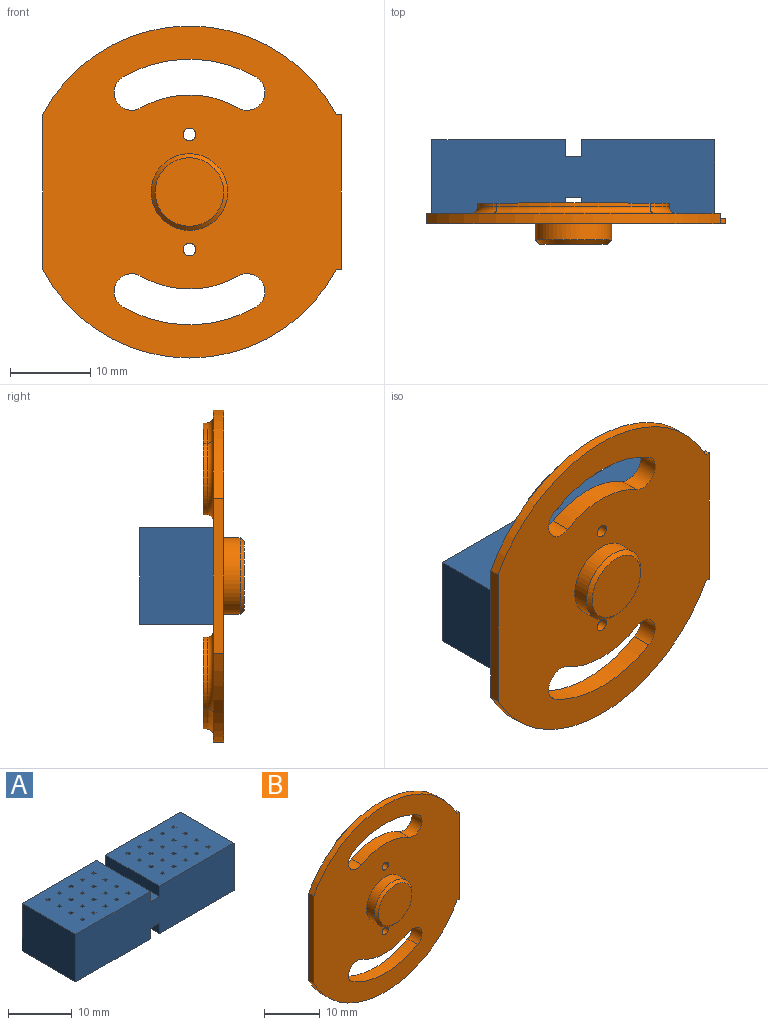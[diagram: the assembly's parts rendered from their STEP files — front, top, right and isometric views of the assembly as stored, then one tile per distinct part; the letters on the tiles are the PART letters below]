
ASSEMBLY  parts=2 mates=1
PART A: 214 faces, bbox 35.2x11.9x9.1 mm
  f0: plane 2.03x0.51mm, normal (0,1,0), area 1mm2, adj f1,f3,f4,f194
  f1: plane 2.03x0.51mm, normal (1,0,0), area 1mm2, adj f0,f2,f4,f194
  f2: plane 2.03x0.51mm, normal (0,-1,0), area 1mm2, adj f1,f3,f4,f194
  f3: plane 2.03x0.51mm, normal (-1,0,0), area 1mm2, adj f0,f2,f4,f194
  f4: plane 0.51x0.51mm, normal (0,0,1), area 0.3mm2, adj f0,f1,f2,f3
  f5: plane 2.03x0.51mm, normal (0,1,0), area 1mm2, adj f6,f8,f9,f194
  f6: plane 2.03x0.51mm, normal (1,0,0), area 1mm2, adj f5,f7,f9,f194
  f7: plane 2.03x0.51mm, normal (0,-1,0), area 1mm2, adj f6,f8,f9,f194
  f8: plane 2.03x0.51mm, normal (-1,0,0), area 1mm2, adj f5,f7,f9,f194
  f9: plane 0.51x0.51mm, normal (0,0,1), area 0.3mm2, adj f5,f6,f7,f8
  f10: plane 2.03x0.51mm, normal (0,1,0), area 1mm2, adj f11,f13,f14,f194
  f11: plane 2.03x0.51mm, normal (1,0,0), area 1mm2, adj f10,f12,f14,f194
  f12: plane 2.03x0.51mm, normal (0,-1,0), area 1mm2, adj f11,f13,f14,f194
  f13: plane 2.03x0.51mm, normal (-1,0,0), area 1mm2, adj f10,f12,f14,f194
  f14: plane 0.51x0.51mm, normal (0,0,1), area 0.3mm2, adj f10,f11,f12,f13
  f15: plane 2.03x0.51mm, normal (0,1,0), area 1mm2, adj f16,f18,f19,f194
  f16: plane 2.03x0.51mm, normal (1,0,0), area 1mm2, adj f15,f17,f19,f194
  f17: plane 2.03x0.51mm, normal (0,-1,0), area 1mm2, adj f16,f18,f19,f194
  f18: plane 2.03x0.51mm, normal (-1,0,0), area 1mm2, adj f15,f17,f19,f194
  f19: plane 0.51x0.51mm, normal (0,0,1), area 0.3mm2, adj f15,f16,f17,f18
  f20: plane 2.03x0.51mm, normal (0,1,0), area 1mm2, adj f21,f23,f24,f194
  f21: plane 2.03x0.51mm, normal (1,0,0), area 1mm2, adj f20,f22,f24,f194
  f22: plane 2.03x0.51mm, normal (0,-1,0), area 1mm2, adj f21,f23,f24,f194
  f23: plane 2.03x0.51mm, normal (-1,0,0), area 1mm2, adj f20,f22,f24,f194
  f24: plane 0.51x0.51mm, normal (0,0,1), area 0.3mm2, adj f20,f21,f22,f23
  f25: plane 2.03x0.51mm, normal (0,1,0), area 1mm2, adj f26,f28,f29,f194
  f26: plane 2.03x0.51mm, normal (1,0,0), area 1mm2, adj f25,f27,f29,f194
  f27: plane 2.03x0.51mm, normal (0,-1,0), area 1mm2, adj f26,f28,f29,f194
  f28: plane 2.03x0.51mm, normal (-1,0,0), area 1mm2, adj f25,f27,f29,f194
  f29: plane 0.51x0.51mm, normal (0,0,1), area 0.3mm2, adj f25,f26,f27,f28
  f30: plane 2.03x0.51mm, normal (0,1,0), area 1mm2, adj f31,f33,f34,f194
  f31: plane 2.03x0.51mm, normal (1,0,0), area 1mm2, adj f30,f32,f34,f194
  f32: plane 2.03x0.51mm, normal (0,-1,0), area 1mm2, adj f31,f33,f34,f194
  f33: plane 2.03x0.51mm, normal (-1,0,0), area 1mm2, adj f30,f32,f34,f194
  f34: plane 0.51x0.51mm, normal (0,0,1), area 0.3mm2, adj f30,f31,f32,f33
  f35: plane 2.03x0.51mm, normal (0,1,0), area 1mm2, adj f36,f38,f39,f194
  f36: plane 2.03x0.51mm, normal (1,0,0), area 1mm2, adj f35,f37,f39,f194
  f37: plane 2.03x0.51mm, normal (0,-1,0), area 1mm2, adj f36,f38,f39,f194
  f38: plane 2.03x0.51mm, normal (-1,0,0), area 1mm2, adj f35,f37,f39,f194
  f39: plane 0.51x0.51mm, normal (0,0,1), area 0.3mm2, adj f35,f36,f37,f38
  f40: plane 2.03x0.51mm, normal (0,1,0), area 1mm2, adj f41,f43,f44,f194
  f41: plane 2.03x0.51mm, normal (1,0,0), area 1mm2, adj f40,f42,f44,f194
  f42: plane 2.03x0.51mm, normal (0,-1,0), area 1mm2, adj f41,f43,f44,f194
  f43: plane 2.03x0.51mm, normal (-1,0,0), area 1mm2, adj f40,f42,f44,f194
  f44: plane 0.51x0.51mm, normal (0,0,1), area 0.3mm2, adj f40,f41,f42,f43
  f45: plane 2.03x0.51mm, normal (0,1,0), area 1mm2, adj f46,f48,f49,f194
  f46: plane 2.03x0.51mm, normal (1,0,0), area 1mm2, adj f45,f47,f49,f194
  f47: plane 2.03x0.51mm, normal (0,-1,0), area 1mm2, adj f46,f48,f49,f194
  f48: plane 2.03x0.51mm, normal (-1,0,0), area 1mm2, adj f45,f47,f49,f194
  f49: plane 0.51x0.51mm, normal (0,0,1), area 0.3mm2, adj f45,f46,f47,f48
  f50: plane 2.03x0.51mm, normal (0,1,0), area 1mm2, adj f51,f53,f54,f194
  f51: plane 2.03x0.51mm, normal (1,0,0), area 1mm2, adj f50,f52,f54,f194
  f52: plane 2.03x0.51mm, normal (0,-1,0), area 1mm2, adj f51,f53,f54,f194
  f53: plane 2.03x0.51mm, normal (-1,0,0), area 1mm2, adj f50,f52,f54,f194
  f54: plane 0.51x0.51mm, normal (0,0,1), area 0.3mm2, adj f50,f51,f52,f53
  f55: plane 2.03x0.51mm, normal (0,1,0), area 1mm2, adj f56,f58,f59,f194
  f56: plane 2.03x0.51mm, normal (1,0,0), area 1mm2, adj f55,f57,f59,f194
  f57: plane 2.03x0.51mm, normal (0,-1,0), area 1mm2, adj f56,f58,f59,f194
  f58: plane 2.03x0.51mm, normal (-1,0,0), area 1mm2, adj f55,f57,f59,f194
  f59: plane 0.51x0.51mm, normal (0,0,1), area 0.3mm2, adj f55,f56,f57,f58
  f60: plane 2.03x0.51mm, normal (0,1,0), area 1mm2, adj f61,f63,f64,f194
  f61: plane 2.03x0.51mm, normal (1,0,0), area 1mm2, adj f60,f62,f64,f194
  f62: plane 2.03x0.51mm, normal (0,-1,0), area 1mm2, adj f61,f63,f64,f194
  f63: plane 2.03x0.51mm, normal (-1,0,0), area 1mm2, adj f60,f62,f64,f194
  f64: plane 0.51x0.51mm, normal (0,0,1), area 0.3mm2, adj f60,f61,f62,f63
  f65: plane 2.03x0.51mm, normal (0,1,0), area 1mm2, adj f66,f68,f69,f194
  f66: plane 2.03x0.51mm, normal (1,0,0), area 1mm2, adj f65,f67,f69,f194
  f67: plane 2.03x0.51mm, normal (0,-1,0), area 1mm2, adj f66,f68,f69,f194
  f68: plane 2.03x0.51mm, normal (-1,0,0), area 1mm2, adj f65,f67,f69,f194
  f69: plane 0.51x0.51mm, normal (0,0,1), area 0.3mm2, adj f65,f66,f67,f68
  f70: plane 2.03x0.51mm, normal (0,1,0), area 1mm2, adj f71,f73,f74,f194
  f71: plane 2.03x0.51mm, normal (1,0,0), area 1mm2, adj f70,f72,f74,f194
  f72: plane 2.03x0.51mm, normal (0,-1,0), area 1mm2, adj f71,f73,f74,f194
  f73: plane 2.03x0.51mm, normal (-1,0,0), area 1mm2, adj f70,f72,f74,f194
  f74: plane 0.51x0.51mm, normal (0,0,1), area 0.3mm2, adj f70,f71,f72,f73
  f75: plane 2.03x0.51mm, normal (0,1,0), area 1mm2, adj f76,f78,f79,f194
  f76: plane 2.03x0.51mm, normal (1,0,0), area 1mm2, adj f75,f77,f79,f194
  f77: plane 2.03x0.51mm, normal (0,-1,0), area 1mm2, adj f76,f78,f79,f194
  f78: plane 2.03x0.51mm, normal (-1,0,0), area 1mm2, adj f75,f77,f79,f194
  f79: plane 0.51x0.51mm, normal (0,0,1), area 0.3mm2, adj f75,f76,f77,f78
  f80: plane 2.03x0.51mm, normal (0,1,0), area 1mm2, adj f81,f83,f84,f194
  f81: plane 2.03x0.51mm, normal (1,0,0), area 1mm2, adj f80,f82,f84,f194
  f82: plane 2.03x0.51mm, normal (0,-1,0), area 1mm2, adj f81,f83,f84,f194
  f83: plane 2.03x0.51mm, normal (-1,0,0), area 1mm2, adj f80,f82,f84,f194
  f84: plane 0.51x0.51mm, normal (0,0,1), area 0.3mm2, adj f80,f81,f82,f83
  f85: plane 2.03x0.51mm, normal (0,1,0), area 1mm2, adj f86,f88,f89,f194
  f86: plane 2.03x0.51mm, normal (1,0,0), area 1mm2, adj f85,f87,f89,f194
  f87: plane 2.03x0.51mm, normal (0,-1,0), area 1mm2, adj f86,f88,f89,f194
  f88: plane 2.03x0.51mm, normal (-1,0,0), area 1mm2, adj f85,f87,f89,f194
  f89: plane 0.51x0.51mm, normal (0,0,1), area 0.3mm2, adj f85,f86,f87,f88
  f90: plane 2.03x0.51mm, normal (0,1,0), area 1mm2, adj f91,f93,f94,f194
  f91: plane 2.03x0.51mm, normal (1,0,0), area 1mm2, adj f90,f92,f94,f194
  f92: plane 2.03x0.51mm, normal (0,-1,0), area 1mm2, adj f91,f93,f94,f194
  f93: plane 2.03x0.51mm, normal (-1,0,0), area 1mm2, adj f90,f92,f94,f194
  f94: plane 0.51x0.51mm, normal (0,0,1), area 0.3mm2, adj f90,f91,f92,f93
  f95: plane 2.03x0.51mm, normal (0,1,0), area 1mm2, adj f96,f98,f99,f190
  f96: plane 2.03x0.51mm, normal (-1,0,0), area 1mm2, adj f95,f97,f99,f190
  f97: plane 2.03x0.51mm, normal (0,-1,0), area 1mm2, adj f96,f98,f99,f190
  f98: plane 2.03x0.51mm, normal (1,0,0), area 1mm2, adj f95,f97,f99,f190
  f99: plane 0.51x0.51mm, normal (0,0,1), area 0.3mm2, adj f95,f96,f97,f98
  f100: plane 2.03x0.51mm, normal (0,1,0), area 1mm2, adj f101,f103,f104,f190
  f101: plane 2.03x0.51mm, normal (-1,0,0), area 1mm2, adj f100,f102,f104,f190
  f102: plane 2.03x0.51mm, normal (0,-1,0), area 1mm2, adj f101,f103,f104,f190
  f103: plane 2.03x0.51mm, normal (1,0,0), area 1mm2, adj f100,f102,f104,f190
  f104: plane 0.51x0.51mm, normal (0,0,1), area 0.3mm2, adj f100,f101,f102,f103
  f105: plane 2.03x0.51mm, normal (0,1,0), area 1mm2, adj f106,f108,f109,f190
  f106: plane 2.03x0.51mm, normal (-1,0,0), area 1mm2, adj f105,f107,f109,f190
  f107: plane 2.03x0.51mm, normal (0,-1,0), area 1mm2, adj f106,f108,f109,f190
  f108: plane 2.03x0.51mm, normal (1,0,0), area 1mm2, adj f105,f107,f109,f190
  f109: plane 0.51x0.51mm, normal (0,0,1), area 0.3mm2, adj f105,f106,f107,f108
  f110: plane 2.03x0.51mm, normal (0,1,0), area 1mm2, adj f111,f113,f114,f190
  f111: plane 2.03x0.51mm, normal (-1,0,0), area 1mm2, adj f110,f112,f114,f190
  f112: plane 2.03x0.51mm, normal (0,-1,0), area 1mm2, adj f111,f113,f114,f190
  f113: plane 2.03x0.51mm, normal (1,0,0), area 1mm2, adj f110,f112,f114,f190
  f114: plane 0.51x0.51mm, normal (0,0,1), area 0.3mm2, adj f110,f111,f112,f113
  f115: plane 2.03x0.51mm, normal (0,1,0), area 1mm2, adj f116,f118,f119,f190
  f116: plane 2.03x0.51mm, normal (-1,0,0), area 1mm2, adj f115,f117,f119,f190
  f117: plane 2.03x0.51mm, normal (0,-1,0), area 1mm2, adj f116,f118,f119,f190
  f118: plane 2.03x0.51mm, normal (1,0,0), area 1mm2, adj f115,f117,f119,f190
  f119: plane 0.51x0.51mm, normal (0,0,1), area 0.3mm2, adj f115,f116,f117,f118
  f120: plane 2.03x0.51mm, normal (0,1,0), area 1mm2, adj f121,f123,f124,f190
  f121: plane 2.03x0.51mm, normal (-1,0,0), area 1mm2, adj f120,f122,f124,f190
  f122: plane 2.03x0.51mm, normal (0,-1,0), area 1mm2, adj f121,f123,f124,f190
  f123: plane 2.03x0.51mm, normal (1,0,0), area 1mm2, adj f120,f122,f124,f190
  f124: plane 0.51x0.51mm, normal (0,0,1), area 0.3mm2, adj f120,f121,f122,f123
  f125: plane 2.03x0.51mm, normal (0,1,0), area 1mm2, adj f126,f128,f129,f190
  f126: plane 2.03x0.51mm, normal (-1,0,0), area 1mm2, adj f125,f127,f129,f190
  f127: plane 2.03x0.51mm, normal (0,-1,0), area 1mm2, adj f126,f128,f129,f190
  f128: plane 2.03x0.51mm, normal (1,0,0), area 1mm2, adj f125,f127,f129,f190
  f129: plane 0.51x0.51mm, normal (0,0,1), area 0.3mm2, adj f125,f126,f127,f128
  f130: plane 2.03x0.51mm, normal (0,1,0), area 1mm2, adj f131,f133,f134,f190
  f131: plane 2.03x0.51mm, normal (-1,0,0), area 1mm2, adj f130,f132,f134,f190
  f132: plane 2.03x0.51mm, normal (0,-1,0), area 1mm2, adj f131,f133,f134,f190
  f133: plane 2.03x0.51mm, normal (1,0,0), area 1mm2, adj f130,f132,f134,f190
  f134: plane 0.51x0.51mm, normal (0,0,1), area 0.3mm2, adj f130,f131,f132,f133
  f135: plane 2.03x0.51mm, normal (0,1,0), area 1mm2, adj f136,f138,f139,f190
  f136: plane 2.03x0.51mm, normal (-1,0,0), area 1mm2, adj f135,f137,f139,f190
  f137: plane 2.03x0.51mm, normal (0,-1,0), area 1mm2, adj f136,f138,f139,f190
  f138: plane 2.03x0.51mm, normal (1,0,0), area 1mm2, adj f135,f137,f139,f190
  f139: plane 0.51x0.51mm, normal (0,0,1), area 0.3mm2, adj f135,f136,f137,f138
  f140: plane 2.03x0.51mm, normal (0,1,0), area 1mm2, adj f141,f143,f144,f190
  f141: plane 2.03x0.51mm, normal (-1,0,0), area 1mm2, adj f140,f142,f144,f190
  f142: plane 2.03x0.51mm, normal (0,-1,0), area 1mm2, adj f141,f143,f144,f190
  f143: plane 2.03x0.51mm, normal (1,0,0), area 1mm2, adj f140,f142,f144,f190
  f144: plane 0.51x0.51mm, normal (0,0,1), area 0.3mm2, adj f140,f141,f142,f143
  f145: plane 2.03x0.51mm, normal (0,1,0), area 1mm2, adj f146,f148,f149,f190
  f146: plane 2.03x0.51mm, normal (-1,0,0), area 1mm2, adj f145,f147,f149,f190
  f147: plane 2.03x0.51mm, normal (0,-1,0), area 1mm2, adj f146,f148,f149,f190
  f148: plane 2.03x0.51mm, normal (1,0,0), area 1mm2, adj f145,f147,f149,f190
  f149: plane 0.51x0.51mm, normal (0,0,1), area 0.3mm2, adj f145,f146,f147,f148
  f150: plane 2.03x0.51mm, normal (0,1,0), area 1mm2, adj f151,f153,f154,f190
  f151: plane 2.03x0.51mm, normal (-1,0,0), area 1mm2, adj f150,f152,f154,f190
  f152: plane 2.03x0.51mm, normal (0,-1,0), area 1mm2, adj f151,f153,f154,f190
  f153: plane 2.03x0.51mm, normal (1,0,0), area 1mm2, adj f150,f152,f154,f190
  f154: plane 0.51x0.51mm, normal (0,0,1), area 0.3mm2, adj f150,f151,f152,f153
  f155: plane 2.03x0.51mm, normal (0,1,0), area 1mm2, adj f156,f158,f159,f190
  f156: plane 2.03x0.51mm, normal (-1,0,0), area 1mm2, adj f155,f157,f159,f190
  f157: plane 2.03x0.51mm, normal (0,-1,0), area 1mm2, adj f156,f158,f159,f190
  f158: plane 2.03x0.51mm, normal (1,0,0), area 1mm2, adj f155,f157,f159,f190
  f159: plane 0.51x0.51mm, normal (0,0,1), area 0.3mm2, adj f155,f156,f157,f158
  f160: plane 2.03x0.51mm, normal (0,1,0), area 1mm2, adj f161,f163,f164,f190
  f161: plane 2.03x0.51mm, normal (-1,0,0), area 1mm2, adj f160,f162,f164,f190
  f162: plane 2.03x0.51mm, normal (0,-1,0), area 1mm2, adj f161,f163,f164,f190
  f163: plane 2.03x0.51mm, normal (1,0,0), area 1mm2, adj f160,f162,f164,f190
  f164: plane 0.51x0.51mm, normal (0,0,1), area 0.3mm2, adj f160,f161,f162,f163
  f165: plane 2.03x0.51mm, normal (0,1,0), area 1mm2, adj f166,f168,f169,f190
  f166: plane 2.03x0.51mm, normal (-1,0,0), area 1mm2, adj f165,f167,f169,f190
  f167: plane 2.03x0.51mm, normal (0,-1,0), area 1mm2, adj f166,f168,f169,f190
  f168: plane 2.03x0.51mm, normal (1,0,0), area 1mm2, adj f165,f167,f169,f190
  f169: plane 0.51x0.51mm, normal (0,0,1), area 0.3mm2, adj f165,f166,f167,f168
  f170: plane 2.03x0.51mm, normal (0,1,0), area 1mm2, adj f171,f173,f174,f190
  f171: plane 2.03x0.51mm, normal (-1,0,0), area 1mm2, adj f170,f172,f174,f190
  f172: plane 2.03x0.51mm, normal (0,-1,0), area 1mm2, adj f171,f173,f174,f190
  f173: plane 2.03x0.51mm, normal (1,0,0), area 1mm2, adj f170,f172,f174,f190
  f174: plane 0.51x0.51mm, normal (0,0,1), area 0.3mm2, adj f170,f171,f172,f173
  f175: plane 2.03x0.51mm, normal (0,1,0), area 1mm2, adj f176,f178,f179,f190
  f176: plane 2.03x0.51mm, normal (-1,0,0), area 1mm2, adj f175,f177,f179,f190
  f177: plane 2.03x0.51mm, normal (0,-1,0), area 1mm2, adj f176,f178,f179,f190
  f178: plane 2.03x0.51mm, normal (1,0,0), area 1mm2, adj f175,f177,f179,f190
  f179: plane 0.51x0.51mm, normal (0,0,1), area 0.3mm2, adj f175,f176,f177,f178
  f180: plane 2.03x0.51mm, normal (0,1,0), area 1mm2, adj f181,f183,f184,f190
  f181: plane 2.03x0.51mm, normal (-1,0,0), area 1mm2, adj f180,f182,f184,f190
  f182: plane 2.03x0.51mm, normal (0,-1,0), area 1mm2, adj f181,f183,f184,f190
  f183: plane 2.03x0.51mm, normal (1,0,0), area 1mm2, adj f180,f182,f184,f190
  f184: plane 0.51x0.51mm, normal (0,0,1), area 0.3mm2, adj f180,f181,f182,f183
  f185: plane 2.03x0.51mm, normal (0,1,0), area 1mm2, adj f186,f188,f189,f190
  f186: plane 2.03x0.51mm, normal (-1,0,0), area 1mm2, adj f185,f187,f189,f190
  f187: plane 2.03x0.51mm, normal (0,-1,0), area 1mm2, adj f186,f188,f189,f190
  f188: plane 2.03x0.51mm, normal (1,0,0), area 1mm2, adj f185,f187,f189,f190
  f189: plane 0.51x0.51mm, normal (0,0,1), area 0.3mm2, adj f185,f186,f187,f188
  f190: plane 16.57x11.94mm, normal (0,0,1), area 192.7mm2, adj f95,f96,f97,f98,f100,f101,f102,f103
  f191: plane 16.57x11.94mm, normal (0,0,-1), area 197.9mm2, adj f195,f196,f197,f203
  f192: plane 16.57x11.94mm, normal (0,0,-1), area 197.9mm2, adj f193,f196,f197,f201
  f193: plane 11.94x9.14mm, normal (1,0,0), area 109.2mm2, adj f192,f194,f196,f197
  f194: plane 16.57x11.94mm, normal (0,0,1), area 192.7mm2, adj f0,f1,f2,f3,f5,f6,f7,f8
  f195: plane 11.94x9.14mm, normal (-1,0,0), area 109.2mm2, adj f190,f191,f196,f197
  f196: plane 35.18x9.14mm, normal (0,-1,0), area 313.4mm2, adj f190,f191,f192,f193,f194,f195,f198,f199
  f197: plane 35.18x9.14mm, normal (0,1,0), area 313.4mm2, adj f190,f191,f192,f193,f194,f195,f198,f199
  f198: plane 11.94x2.03mm, normal (1,0,0), area 24.3mm2, adj f190,f196,f197,f199
  f199: plane 11.94x2.03mm, normal (0,0,1), area 24.3mm2, adj f196,f197,f198,f200
  f200: plane 11.94x2.03mm, normal (-1,0,0), area 24.3mm2, adj f194,f196,f197,f199
  f201: plane 11.94x2.03mm, normal (-1,0,0), area 24.3mm2, adj f192,f196,f197,f202
  f202: plane 11.94x2.03mm, normal (0,0,-1), area 24.3mm2, adj f196,f197,f201,f203
  f203: plane 11.94x2.03mm, normal (1,0,0), area 24.3mm2, adj f191,f196,f197,f202
  f204: plane 2.03x0.51mm, normal (0,1,0), area 1mm2, adj f190,f205,f207,f208
  f205: plane 2.03x0.51mm, normal (-1,0,0), area 1mm2, adj f190,f204,f206,f208
  f206: plane 2.03x0.51mm, normal (0,-1,0), area 1mm2, adj f190,f205,f207,f208
  f207: plane 2.03x0.51mm, normal (1,0,0), area 1mm2, adj f190,f204,f206,f208
  f208: plane 0.51x0.51mm, normal (0,0,1), area 0.3mm2, adj f204,f205,f206,f207
  f209: plane 2.03x0.51mm, normal (0,1,0), area 1mm2, adj f194,f210,f212,f213
  f210: plane 2.03x0.51mm, normal (-1,0,0), area 1mm2, adj f194,f209,f211,f213
  f211: plane 2.03x0.51mm, normal (0,-1,0), area 1mm2, adj f194,f210,f212,f213
  f212: plane 2.03x0.51mm, normal (1,0,0), area 1mm2, adj f194,f209,f211,f213
  f213: plane 0.51x0.51mm, normal (0,0,1), area 0.3mm2, adj f209,f210,f211,f212
PART B: 41 faces, bbox 37.1x5.2x44.2 mm
  f0: plane 19.25x0.64mm, normal (1,0,0), area 12.2mm2, adj f1,f3,f4,f37
  f1: cylinder r=20.64mm len=36.51mm, axis (0,1,0), area 56.9mm2, adj f0,f2,f3,f35,f39
  f2: plane 41.28x37.15mm, normal (0,-1,0), area 1049.1mm2, adj f1,f4,f5,f7,f14,f15,f16,f17
  f3: plane 41.28x36.51mm, normal (0,1,0), area 745.7mm2, adj f0,f1,f4,f5,f18,f19,f20,f21
  f4: cylinder r=20.64mm len=36.51mm, axis (0,1,0), area 56.9mm2, adj f0,f2,f3,f35,f38
  f5: cylinder r=0.79mm len=1.59mm, axis (0,1,0), area 6.3mm2, adj f2,f3
  f6: plane 23.81x11.44mm, normal (0,1,0), area 131.7mm2, adj f22,f23,f24,f25,f26,f27,f28,f29
  f7: cylinder r=4.76mm len=9.53mm, axis (0,1,0), area 60.8mm2, adj f2,f36
  f8: plane 8.51x8.51mm, normal (0,-1,0), area 56.9mm2, adj f36
  f9: cylinder r=19.05mm len=19.05mm, axis (0,-1,0), area 9.5mm2, adj f10,f12,f13,f21
  f10: cylinder r=4.76mm len=8.89mm, axis (0,-1,0), area 7.1mm2, adj f9,f11,f13,f19
  f11: cylinder r=9.53mm len=9.53mm, axis (0,-1,0), area 4.8mm2, adj f10,f12,f13,f18
  f12: cylinder r=4.76mm len=8.89mm, axis (0,-1,0), area 7.1mm2, adj f9,f11,f13,f20
  f13: plane 23.81x11.44mm, normal (0,1,0), area 131.7mm2, adj f9,f10,f11,f12,f14,f15,f16,f17
  f14: cylinder r=2.22mm len=4.15mm, axis (0,1,0), area 17.7mm2, adj f2,f13,f15,f16
  f15: cylinder r=16.51mm len=16.51mm, axis (0,1,0), area 43.9mm2, adj f2,f13,f14,f17
  f16: cylinder r=12.06mm len=12.07mm, axis (0,1,0), area 32.1mm2, adj f2,f13,f14,f17
  f17: cylinder r=2.22mm len=4.15mm, axis (0,1,0), area 17.7mm2, adj f2,f13,f15,f16
  f18: torus R=8.73mm, axis (0,-1,0), area 12.1mm2, adj f3,f11,f19,f20
  f19: torus R=5.56mm, axis (0,-1,0), area 19.8mm2, adj f3,f10,f18,f21
  f20: torus R=5.56mm, axis (0,-1,0), area 19.8mm2, adj f3,f12,f18,f21
  f21: torus R=19.84mm, axis (0,-1,0), area 25.2mm2, adj f3,f9,f19,f20
  f22: cylinder r=19.05mm len=19.05mm, axis (0,-1,0), area 9.5mm2, adj f6,f23,f25,f33
  f23: cylinder r=4.76mm len=8.89mm, axis (0,-1,0), area 7.1mm2, adj f6,f22,f24,f32
  f24: cylinder r=9.53mm len=9.53mm, axis (0,-1,0), area 4.8mm2, adj f6,f23,f25,f30
  f25: cylinder r=4.76mm len=8.89mm, axis (0,-1,0), area 7.1mm2, adj f6,f22,f24,f31
  f26: cylinder r=16.51mm len=16.51mm, axis (0,1,0), area 43.9mm2, adj f2,f6,f27,f29
  f27: cylinder r=2.22mm len=4.15mm, axis (0,1,0), area 17.7mm2, adj f2,f6,f26,f28
  f28: cylinder r=12.06mm len=12.07mm, axis (0,1,0), area 32.1mm2, adj f2,f6,f27,f29
  f29: cylinder r=2.22mm len=4.15mm, axis (0,1,0), area 17.7mm2, adj f2,f6,f26,f28
  f30: torus R=8.73mm, axis (0,-1,0), area 12.1mm2, adj f3,f24,f31,f32
  f31: torus R=5.56mm, axis (0,-1,0), area 19.8mm2, adj f3,f25,f30,f33
  f32: torus R=5.56mm, axis (0,-1,0), area 19.8mm2, adj f3,f23,f30,f33
  f33: torus R=19.84mm, axis (0,-1,0), area 25.2mm2, adj f3,f22,f31,f32
  f34: cylinder r=0.79mm len=1.59mm, axis (0,1,0), area 6.3mm2, adj f2,f3
  f35: plane 19.25x1.27mm, normal (-1,0,0), area 24.4mm2, adj f1,f2,f3,f4
  f36: cone r=4.25mm half-angle=45deg, axis (0,1,0), area 20.4mm2, adj f7,f8
  f37: plane 19.25x0.64mm, normal (0,1,0), area 12.2mm2, adj f0,f38,f39,f40
  f38: plane 0.64x0.64mm, normal (0,0,1), area 0.4mm2, adj f2,f4,f37,f40
  f39: plane 0.64x0.64mm, normal (0,0,-1), area 0.4mm2, adj f1,f2,f37,f40
  f40: plane 19.25x0.64mm, normal (1,0,0), area 12.2mm2, adj f2,f37,f38,f39
PLACE A rot(axis=(-1,0,0),90deg) t=(0,4.57,0)mm
PLACE B at identity
MATE fastened A.f191 <-> B.f11  axis (0,-1,0) through (0,0,0)mm
